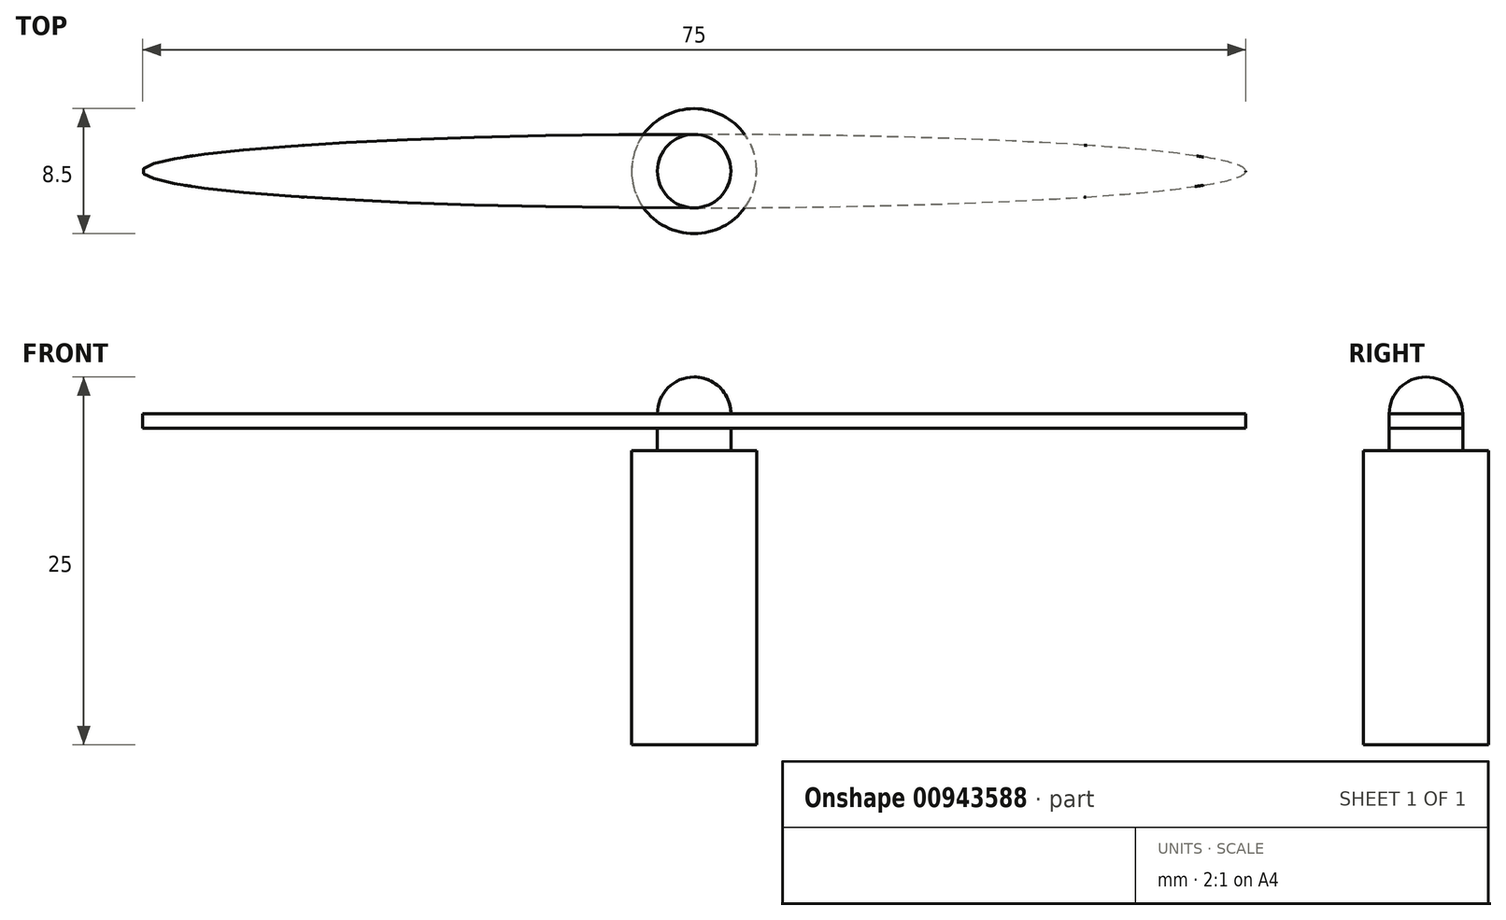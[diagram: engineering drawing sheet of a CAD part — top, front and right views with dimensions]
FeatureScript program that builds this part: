
annotation { "Feature Type Name" : "Feature", "Feature Type Description" : "" }
export const myFeature = defineFeature(function(context is Context, id is Id, definition is map)
    precondition{}
    {
        {
            var Q0;
            Q0=qCreatedBy(makeId("Top.planeOp"),FACE);
            var sketch = newSketch(context, id + "F0", { "sketchPlane" : qUnion([Q0])});
            skCircle(sketch, "E0", {"center": v(0, 0) * mm, "radius": 4.25 * mm});
            skSolve(sketch);
        }
        {
            var Q0;
            Q0 = qSketchRegion(id + "F0", true);
            var Q1;
            Q1=sQuery(id+"F0.wireOp",EDGE,"E0");
            extrude(context, id + "F1", {"entities" : qUnion([Q0]), "surfaceEntities" : qUnion([Q1]), "depth" : 20 * mm, "offsetDistance" : 25 * mm});
        }
        {
            var Q0;
            Q0=makeQuery(id+"F1.opExtrude","CAP_FACE",FACE,{"disambiguationData":[OSD([sQuery(id+"F0.wireOp",EDGE,"E0")])],"isStart":false});
            var sketch = newSketch(context, id + "F2", { "sketchPlane" : qUnion([Q0])});
            skCircle(sketch, "E1", {"center": v(0, 0) * mm, "radius": 2.5 * mm});
            skSolve(sketch);
        }
        {
            var Q0;
            Q0 = qSketchRegion(id + "F2", true);
            extrude(context, id + "F3", {"entities" : qUnion([Q0]), "depth" : 5 * mm, "offsetDistance" : 25 * mm});
        }
        {
            var Q0;
            Q0=makeQuery(id+"F3.opExtrude","CAP_EDGE",EDGE,{"disambiguationData":[OSD([sQuery(id+"F2.wireOp",EDGE,"E1")])],"isStart":false});
            fillet(context, id + "F4", {"entities" : qUnion([Q0]), "radius" : 2.5 * mm, "tangentPropagation" : true, "allowEdgeOverflow" : false});
        }
        {
            var Q0;
            Q0=makeQuery(id+"F1.opExtrude","CAP_FACE",FACE,{"disambiguationData":[OSD([sQuery(id+"F0.wireOp",EDGE,"E0")])],"isStart":false});
            cPlane(context, id + "F5", {"entities" : qUnion([Q0]), "cplaneType" : CPlaneType.OFFSET, "offset" : 2.5 * mm, "width" : 150 * mm, "height" : 150 * mm});
        }
        {
            var Q0;
            Q0=qCreatedBy(id+"F5.planeOp",FACE);
            var sketch = newSketch(context, id + "F6", { "sketchPlane" : qUnion([Q0])});
            skEllipse(sketch, "E2", {"center": v(0, 0) * mm, "majorRadius": 37.5 * mm, "minorRadius": 2.5 * mm, "majorAxis": v(-1, 0)});
            skSolve(sketch);
        }
        {
            var Q0;
            Q0 = qSketchRegion(id + "F6", true);
            extrude(context, id + "F7", {"entities" : qUnion([Q0]), "operationType" : NewBodyOperationType.ADD, "oppositeDirection" : true, "depth" : 1 * mm, "offsetDistance" : 25 * mm});
        }
    });
